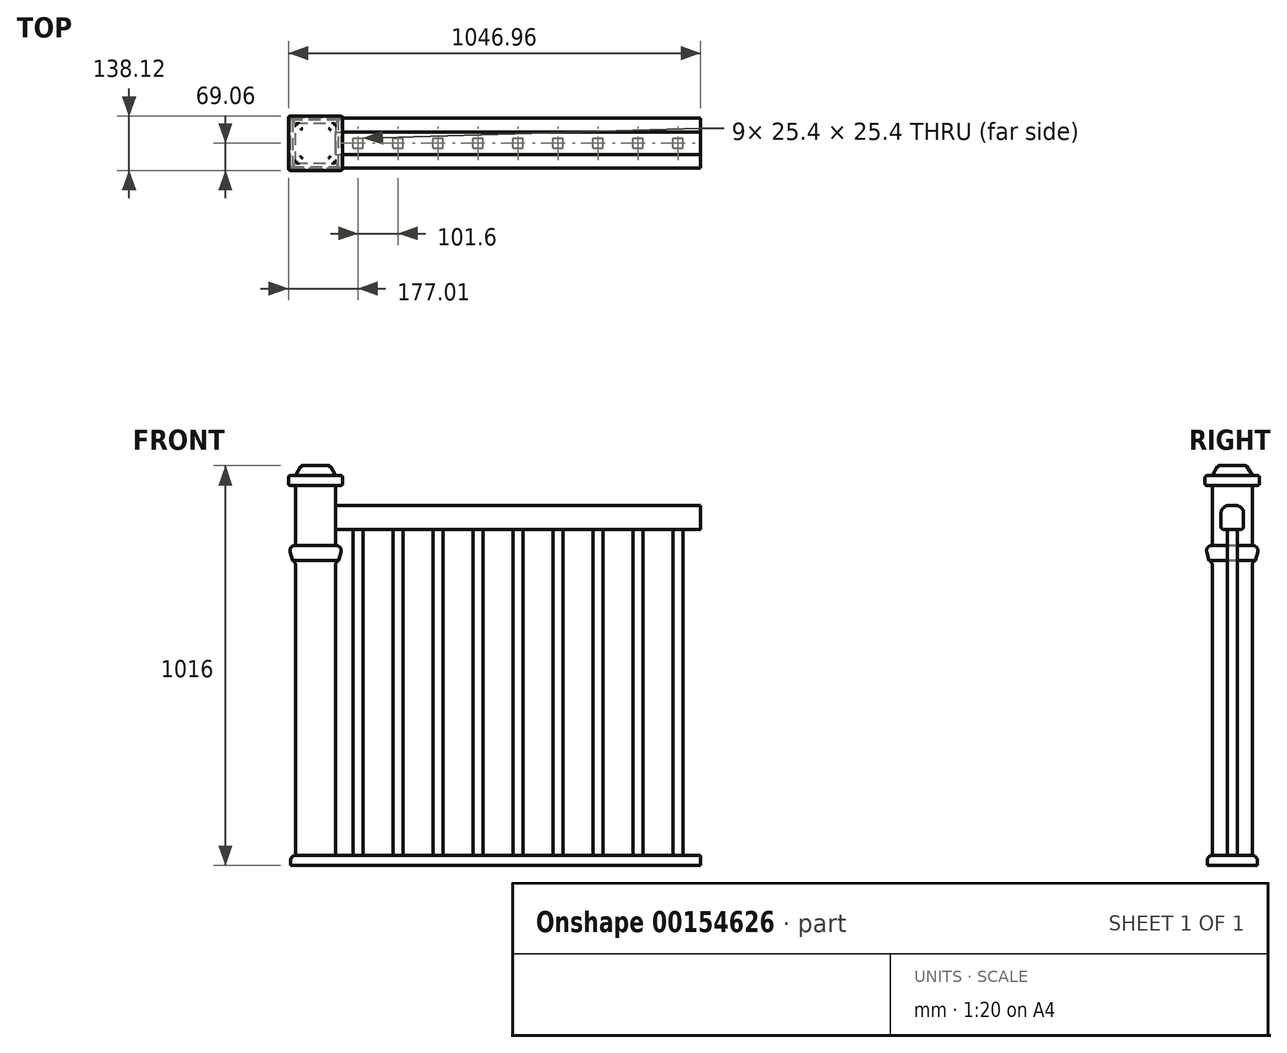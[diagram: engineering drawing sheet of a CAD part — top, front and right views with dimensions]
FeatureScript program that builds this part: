
annotation { "Feature Type Name" : "Feature", "Feature Type Description" : "" }
export const myFeature = defineFeature(function(context is Context, id is Id, definition is map)
    precondition{}
    {
        {
            var Q0;
            Q0=qCreatedBy(makeId("Front.planeOp"),FACE);
            var sketch = newSketch(context, id + "F0", { "sketchPlane" : qUnion([Q0])});
            skLineSegment(sketch, "E0", {"start": v(0, 0) * mm, "end": v(0, 787.4) * mm, "construction": true});
            skLineSegment(sketch, "E1", {"start": v(0, 787.4) * mm, "end": v(1028.7, 787.4) * mm, "construction": true});
            skLineSegment(sketch, "E2", {"start": v(1028.7, 1191.24) * mm, "end": v(1028.7, 0) * mm, "construction": true});
            skLineSegment(sketch, "E3", {"start": v(0, 0) * mm, "end": v(1028.7, 0) * mm, "construction": true});
            skLineSegment(sketch, "E4", {"start": v(1028.7, 1191.24) * mm, "end": v(1247.94, 1191.24) * mm, "construction": true});
            skLineSegment(sketch, "E5", {"start": v(1247.94, 0) * mm, "end": v(1247.94, 1191.24) * mm, "construction": true});
            skLineSegment(sketch, "E6", {"start": v(1028.7, 0) * mm, "end": v(1247.94, 0) * mm, "construction": true});
            skSolve(sketch);
        }
        {
            var Q0;
            Q0=qCreatedBy(makeId("Front.planeOp"),FACE);
            var sketch = newSketch(context, id + "F1", { "sketchPlane" : qUnion([Q0])});
            skLineSegment(sketch, "E7", {"start": v(101.6, 0) * mm, "end": v(0, 0) * mm});
            skLineSegment(sketch, "E8", {"start": v(101.6, 25.4) * mm, "end": v(101.6, 990.6) * mm});
            skLineSegment(sketch, "E9", {"start": v(101.6, 990.6) * mm, "end": v(0, 990.6) * mm});
            skLineSegment(sketch, "E10", {"start": v(0, 990.6) * mm, "end": v(0, 25.4) * mm});
            skLineSegment(sketch, "E11", {"start": v(101.6, 854.08) * mm, "end": v(1028.7, 854.08) * mm});
            skLineSegment(sketch, "E12.0", {"start": v(101.6, 914.4) * mm, "end": v(1028.7, 914.4) * mm});
            skLineSegment(sketch, "E13", {"start": v(1028.7, 914.4) * mm, "end": v(1028.7, 854.08) * mm});
            skLineSegment(sketch, "E14.bottom", {"start": v(-12.7, 25.4) * mm, "end": v(1028.7, 25.4) * mm});
            skLineSegment(sketch, "E14.top", {"start": v(-12.7, 0) * mm, "end": v(1028.7, 0) * mm});
            skLineSegment(sketch, "E14.left", {"start": v(-12.7, 25.4) * mm, "end": v(-12.7, 0) * mm});
            skLineSegment(sketch, "E14.right", {"start": v(1028.7, 25.4) * mm, "end": v(1028.7, 0) * mm});
            skLineSegment(sketch, "E15", {"start": v(146.05, 854.08) * mm, "end": v(146.05, 25.4) * mm});
            skLineSegment(sketch, "E16", {"start": v(171.45, 854.08) * mm, "end": v(171.45, 25.4) * mm});
            skLineSegment(sketch, "E17", {"start": v(247.65, 854.08) * mm, "end": v(247.65, 25.4) * mm});
            skLineSegment(sketch, "E18", {"start": v(273.05, 854.08) * mm, "end": v(273.05, 25.4) * mm});
            skLineSegment(sketch, "E19.direction1", {"start": v(146.05, 25.4) * mm, "end": v(1028.7, 25.4) * mm, "construction": true});
            skLineSegment(sketch, "E20.1.0.0", {"start": v(374.65, 854.08) * mm, "end": v(374.65, 25.4) * mm});
            skLineSegment(sketch, "E20.1.0.1", {"start": v(349.25, 854.08) * mm, "end": v(349.25, 25.4) * mm});
            skLineSegment(sketch, "E20.2.0.0", {"start": v(476.25, 854.08) * mm, "end": v(476.25, 25.4) * mm});
            skLineSegment(sketch, "E20.2.0.1", {"start": v(450.85, 854.08) * mm, "end": v(450.85, 25.4) * mm});
            skLineSegment(sketch, "E20.3.0.0", {"start": v(577.85, 854.08) * mm, "end": v(577.85, 25.4) * mm});
            skLineSegment(sketch, "E20.3.0.1", {"start": v(552.45, 854.08) * mm, "end": v(552.45, 25.4) * mm});
            skLineSegment(sketch, "E20.4.0.0", {"start": v(679.45, 854.08) * mm, "end": v(679.45, 25.4) * mm});
            skLineSegment(sketch, "E20.4.0.1", {"start": v(654.05, 854.08) * mm, "end": v(654.05, 25.4) * mm});
            skLineSegment(sketch, "E20.5.0.0", {"start": v(781.05, 854.08) * mm, "end": v(781.05, 25.4) * mm});
            skLineSegment(sketch, "E20.5.0.1", {"start": v(755.65, 854.08) * mm, "end": v(755.65, 25.4) * mm});
            skLineSegment(sketch, "E20.6.0.0", {"start": v(882.65, 854.08) * mm, "end": v(882.65, 25.4) * mm});
            skLineSegment(sketch, "E20.6.0.1", {"start": v(857.25, 854.08) * mm, "end": v(857.25, 25.4) * mm});
            skLineSegment(sketch, "E20.7.0.0", {"start": v(984.25, 854.08) * mm, "end": v(984.25, 25.4) * mm});
            skLineSegment(sketch, "E20.7.0.1", {"start": v(958.85, 854.08) * mm, "end": v(958.85, 25.4) * mm});
            skLineSegment(sketch, "E20.direction1", {"start": v(247.65, 25.4) * mm, "end": v(349.25, 25.4) * mm, "construction": true});
            skSolve(sketch);
        }
        {
            var Q0;
            {var subQ0=sQuery(id+"F1.wireOp",EDGE,"E9");Q0=makeQuery(id+"F1.imprint","IMPRINT",FACE,{"disambiguationData":[TD([[makeQuery(id+"F1.imprint","IMPRINT",EDGE,{"derivedFrom":subQ0}),1.0]])]});}
            extrude(context, id + "F2", {"entities" : qUnion([Q0]), "endBound" : BoundingType.SYMMETRIC, "depth" : 101.6 * mm});
        }
        {
            var Q0;
            {var subQ25=sQuery(id+"F1.wireOp",EDGE,"E12.0");Q0=makeQuery(id+"F1.imprint","IMPRINT",FACE,{"disambiguationData":[TD([[makeQuery(id+"F1.imprint","IMPRINT",EDGE,{"derivedFrom":subQ25}),-1.0]])]});}
            extrude(context, id + "F3", {"entities" : qUnion([Q0]), "operationType" : NewBodyOperationType.ADD, "depth" : 25.4 * mm});
        }
        {
            var Q0;
            Q0=makeQuery(id+"F2.opExtrude","SWEPT_BODY",BODY,{"disambiguationData":[OSD([sQuery(id+"F1.wireOp",EDGE,"E8"),sQuery(id+"F1.wireOp",EDGE,"E9"),sQuery(id+"F1.wireOp",EDGE,"E10"),sQuery(id+"F1.wireOp",EDGE,"E14.bottom")])]});
            deleteBodies(context, id + "F4", {"entities" : qUnion([Q0])});
        }
        {
            var Q0;
            {var subQ0=sQuery(id+"F1.wireOp",EDGE,"E9");Q0=makeQuery(id+"F1.imprint","IMPRINT",FACE,{"disambiguationData":[TD([[makeQuery(id+"F1.imprint","IMPRINT",EDGE,{"derivedFrom":subQ0}),1.0]])]});}
            extrude(context, id + "F5", {"entities" : qUnion([Q0]), "endBound" : BoundingType.SYMMETRIC, "depth" : 101.6 * mm});
        }
        {
            var Q0;
            {var subQ25=sQuery(id+"F1.wireOp",EDGE,"E12.0");Q0=makeQuery(id+"F1.imprint","IMPRINT",FACE,{"disambiguationData":[TD([[makeQuery(id+"F1.imprint","IMPRINT",EDGE,{"derivedFrom":subQ25}),-1.0]])]});}
            extrude(context, id + "F6", {"entities" : qUnion([Q0]), "operationType" : NewBodyOperationType.ADD, "endBound" : BoundingType.SYMMETRIC, "depth" : 57.15 * mm});
        }
        {
            var Q0;
            {var subQ24=sQuery(id+"F1.wireOp",EDGE,"E14.left");Q0=makeQuery(id+"F1.imprint","IMPRINT",FACE,{"disambiguationData":[TD([[makeQuery(id+"F1.imprint","IMPRINT",EDGE,{"derivedFrom":subQ24}),1.0]])]});}
            extrude(context, id + "F7", {"entities" : qUnion([Q0]), "operationType" : NewBodyOperationType.ADD, "endBound" : BoundingType.SYMMETRIC, "depth" : 127 * mm});
        }
        {
            var Q0;
            {var subQ0=sQuery(id+"F1.wireOp",EDGE,"E15");Q0=makeQuery(id+"F1.imprint","IMPRINT",FACE,{"disambiguationData":[TD([[makeQuery(id+"F1.imprint","IMPRINT",EDGE,{"derivedFrom":subQ0}),1.0]])]});}
            var Q1;
            {var subQ0=sQuery(id+"F1.wireOp",EDGE,"E17");Q1=makeQuery(id+"F1.imprint","IMPRINT",FACE,{"disambiguationData":[TD([[makeQuery(id+"F1.imprint","IMPRINT",EDGE,{"derivedFrom":subQ0}),1.0]])]});}
            var Q2;
            {var subQ0=sQuery(id+"F1.wireOp",EDGE,"E20.1.0.0");Q2=makeQuery(id+"F1.imprint","IMPRINT",FACE,{"disambiguationData":[TD([[makeQuery(id+"F1.imprint","IMPRINT",EDGE,{"derivedFrom":subQ0}),-1.0]])]});}
            var Q3;
            {var subQ0=sQuery(id+"F1.wireOp",EDGE,"E20.2.0.0");Q3=makeQuery(id+"F1.imprint","IMPRINT",FACE,{"disambiguationData":[TD([[makeQuery(id+"F1.imprint","IMPRINT",EDGE,{"derivedFrom":subQ0}),-1.0]])]});}
            var Q4;
            {var subQ0=sQuery(id+"F1.wireOp",EDGE,"E20.3.0.0");Q4=makeQuery(id+"F1.imprint","IMPRINT",FACE,{"disambiguationData":[TD([[makeQuery(id+"F1.imprint","IMPRINT",EDGE,{"derivedFrom":subQ0}),-1.0]])]});}
            var Q5;
            {var subQ0=sQuery(id+"F1.wireOp",EDGE,"E20.4.0.0");Q5=makeQuery(id+"F1.imprint","IMPRINT",FACE,{"disambiguationData":[TD([[makeQuery(id+"F1.imprint","IMPRINT",EDGE,{"derivedFrom":subQ0}),-1.0]])]});}
            var Q6;
            {var subQ0=sQuery(id+"F1.wireOp",EDGE,"E20.5.0.0");Q6=makeQuery(id+"F1.imprint","IMPRINT",FACE,{"disambiguationData":[TD([[makeQuery(id+"F1.imprint","IMPRINT",EDGE,{"derivedFrom":subQ0}),-1.0]])]});}
            var Q7;
            {var subQ0=sQuery(id+"F1.wireOp",EDGE,"E20.6.0.0");Q7=makeQuery(id+"F1.imprint","IMPRINT",FACE,{"disambiguationData":[TD([[makeQuery(id+"F1.imprint","IMPRINT",EDGE,{"derivedFrom":subQ0}),-1.0]])]});}
            var Q8;
            {var subQ0=sQuery(id+"F1.wireOp",EDGE,"E20.7.0.0");Q8=makeQuery(id+"F1.imprint","IMPRINT",FACE,{"disambiguationData":[TD([[makeQuery(id+"F1.imprint","IMPRINT",EDGE,{"derivedFrom":subQ0}),-1.0]])]});}
            var Q9;
            {var subQ0=sQuery(id+"F1.wireOp",EDGE,"E20.8.0.0");Q9=makeQuery(id+"F1.imprint","IMPRINT",FACE,{"disambiguationData":[TD([[makeQuery(id+"F1.imprint","IMPRINT",EDGE,{"derivedFrom":subQ0}),-1.0]])]});}
            var Q10;
            {var subQ0=sQuery(id+"F1.wireOp",EDGE,"E20.9.0.0");Q10=makeQuery(id+"F1.imprint","IMPRINT",FACE,{"disambiguationData":[TD([[makeQuery(id+"F1.imprint","IMPRINT",EDGE,{"derivedFrom":subQ0}),-1.0]])]});}
            var Q11;
            {var subQ0=sQuery(id+"F1.wireOp",EDGE,"E20.10.0.0");Q11=makeQuery(id+"F1.imprint","IMPRINT",FACE,{"disambiguationData":[TD([[makeQuery(id+"F1.imprint","IMPRINT",EDGE,{"derivedFrom":subQ0}),-1.0]])]});}
            extrude(context, id + "F8", {"entities" : qUnion([Q0, Q1, Q2, Q3, Q4, Q5, Q6, Q7, Q8, Q9, Q10, Q11]), "operationType" : NewBodyOperationType.ADD, "endBound" : BoundingType.SYMMETRIC, "depth" : 25.4 * mm});
        }
        {
            var Q0;
            Q0=makeQuery(id+"F5.opExtrude","SWEPT_FACE",FACE,{"disambiguationData":[OSD([sQuery(id+"F1.wireOp",EDGE,"E9")])]});
            extrude(context, id + "F18", {"entities" : qUnion([Q0]), "operationType" : NewBodyOperationType.ADD, "depth" : 25.4 * mm, "hasDraft" : true, "draftAngle" : 30 * degree, "draftPullDirection" : true});
        }
        {
            var Q0;
            {var subQ0=sQuery(id+"F1.wireOp",EDGE,"E9");var subQ1=sQuery(id+"F1.wireOp",EDGE,"E8");var subQ2=makeQuery(id+"F5.opExtrude","CAP_VERTEX",VERTEX,{"disambiguationData":[OSD([subQ1,subQ0])],"isStart":false});Q0=makeQuery(id+"F18.boolean.opBoolean","MERGE",VERTEX,{"derivedFrom":[subQ2,makeQuery(id+"F18.opExtrude","CAP_VERTEX",VERTEX,{"disambiguationData":[OSD([subQ1,subQ0]),TDD([subQ2])],"isStart":true})]});}
            var Q1;
            {var subQ0=sQuery(id+"F1.wireOp",EDGE,"E9");var subQ1=sQuery(id+"F1.wireOp",EDGE,"E8");var subQ2=makeQuery(id+"F5.opExtrude","CAP_VERTEX",VERTEX,{"disambiguationData":[OSD([subQ1,subQ0])],"isStart":true});Q1=makeQuery(id+"F18.boolean.opBoolean","MERGE",VERTEX,{"derivedFrom":[subQ2,makeQuery(id+"F18.opExtrude","CAP_VERTEX",VERTEX,{"disambiguationData":[OSD([subQ1,subQ0]),TDD([subQ2])],"isStart":true})]});}
            var Q2;
            {var subQ0=sQuery(id+"F1.wireOp",EDGE,"E10");var subQ1=sQuery(id+"F1.wireOp",EDGE,"E9");var subQ2=makeQuery(id+"F5.opExtrude","CAP_VERTEX",VERTEX,{"disambiguationData":[OSD([subQ1,subQ0])],"isStart":false});Q2=makeQuery(id+"F18.boolean.opBoolean","MERGE",VERTEX,{"derivedFrom":[subQ2,makeQuery(id+"F18.opExtrude","CAP_VERTEX",VERTEX,{"disambiguationData":[OSD([subQ1,subQ0]),TDD([subQ2])],"isStart":true})]});}
            cPlane(context, id + "F9", {"entities" : qUnion([Q0, Q1, Q2]), "cplaneType" : CPlaneType.THREE_POINT, "offset" : 25.4 * mm, "width" : 152.4 * mm, "height" : 152.4 * mm});
        }
        {
            var Q0;
            Q0=qCreatedBy(id+"F9.planeOp",FACE);
            var sketch = newSketch(context, id + "F19", { "sketchPlane" : qUnion([Q0])});
            skLineSegment(sketch, "E21.bottom", {"start": v(119.86, 69.06) * mm, "end": v(-18.26, 69.06) * mm});
            skLineSegment(sketch, "E21.top", {"start": v(119.86, -69.06) * mm, "end": v(-18.26, -69.06) * mm});
            skLineSegment(sketch, "E21.left", {"start": v(119.86, 69.06) * mm, "end": v(119.86, -69.06) * mm});
            skLineSegment(sketch, "E21.right", {"start": v(-18.26, 69.06) * mm, "end": v(-18.26, -69.06) * mm});
            skPoint(sketch, "E21.middle", {"position": v(50.8, 0) * mm});
            skLineSegment(sketch, "E22", {"start": v(14.66, -36.14) * mm, "end": v(86.94, 36.14) * mm, "construction": true});
            skLineSegment(sketch, "E23", {"start": v(86.94, 36.14) * mm, "end": v(14.66, -36.14) * mm, "construction": true});
            skSolve(sketch);
        }
        {
            var Q0;
            Q0=makeQuery(id+"F19.imprint","IMPRINT",FACE,{"disambiguationData":[TD([[makeQuery(id+"F19.imprint","IMPRINT",EDGE,{"derivedFrom":sQuery(id+"F19.wireOp",EDGE,"E21.bottom")}),1.0]])]});
            extrude(context, id + "F10", {"entities" : qUnion([Q0]), "operationType" : NewBodyOperationType.ADD, "depth" : 25.4 * mm});
        }
        {
            var Q0;
            Q0=makeQuery(id+"F10.opExtrude","CAP_FACE",FACE,{"disambiguationData":[OSD([sQuery(id+"F19.wireOp",EDGE,"E21.bottom"),sQuery(id+"F19.wireOp",EDGE,"E21.top"),sQuery(id+"F19.wireOp",EDGE,"E21.left"),sQuery(id+"F19.wireOp",EDGE,"E21.right")])],"isStart":false});
            cPlane(context, id + "F11", {"entities" : qUnion([Q0]), "cplaneType" : CPlaneType.OFFSET, "offset" : 152.4 * mm, "width" : 152.4 * mm, "height" : 152.4 * mm});
        }
        {
            var Q0;
            Q0=qCreatedBy(id+"F11.planeOp",FACE);
            var sketch = newSketch(context, id + "F12", { "sketchPlane" : qUnion([Q0])});
            skLineSegment(sketch, "E24.bottom", {"start": v(-18.26, 69.06) * mm, "end": v(119.86, 69.06) * mm});
            skLineSegment(sketch, "E24.top", {"start": v(-18.26, -69.06) * mm, "end": v(119.86, -69.06) * mm});
            skLineSegment(sketch, "E24.left", {"start": v(-18.26, 69.06) * mm, "end": v(-18.26, -69.06) * mm});
            skLineSegment(sketch, "E24.right", {"start": v(119.86, 69.06) * mm, "end": v(119.86, -69.06) * mm});
            skSolve(sketch);
        }
        {
            var Q0;
            Q0 = qSketchRegion(id + "F12", true);
            extrude(context, id + "F13", {"entities" : qUnion([Q0]), "operationType" : NewBodyOperationType.ADD, "depth" : 38.1 * mm, "hasDraft" : true, "draftAngle" : 15 * degree, "draftPullDirection" : true});
        }
        {
            var Q0;
            Q0=makeQuery(id+"F13.boolean.opBoolean","INTERSECT",EDGE,{"derivedFrom":[makeQuery(id+"F5.opExtrude","CAP_FACE",FACE,{"disambiguationData":[OSD([sQuery(id+"F1.wireOp",EDGE,"E8"),sQuery(id+"F1.wireOp",EDGE,"E9"),sQuery(id+"F1.wireOp",EDGE,"E10"),sQuery(id+"F1.wireOp",EDGE,"E14.bottom")])],"isStart":false}),makeQuery(id+"F13.opExtrude","CAP_FACE",FACE,{"disambiguationData":[OSD([sQuery(id+"F12.wireOp",EDGE,"E24.bottom"),sQuery(id+"F12.wireOp",EDGE,"E24.top"),sQuery(id+"F12.wireOp",EDGE,"E24.left"),sQuery(id+"F12.wireOp",EDGE,"E24.right")])],"isStart":false})]});
            var Q1;
            Q1=makeQuery(id+"F13.boolean.opBoolean","INTERSECT",EDGE,{"derivedFrom":[makeQuery(id+"F5.opExtrude","SWEPT_FACE",FACE,{"disambiguationData":[OSD([sQuery(id+"F1.wireOp",EDGE,"E10")])]}),makeQuery(id+"F13.opExtrude","CAP_FACE",FACE,{"disambiguationData":[OSD([sQuery(id+"F12.wireOp",EDGE,"E24.bottom"),sQuery(id+"F12.wireOp",EDGE,"E24.top"),sQuery(id+"F12.wireOp",EDGE,"E24.left"),sQuery(id+"F12.wireOp",EDGE,"E24.right")])],"isStart":false})]});
            var Q2;
            Q2=makeQuery(id+"F13.boolean.opBoolean","INTERSECT",EDGE,{"derivedFrom":[makeQuery(id+"F5.opExtrude","CAP_FACE",FACE,{"disambiguationData":[OSD([sQuery(id+"F1.wireOp",EDGE,"E8"),sQuery(id+"F1.wireOp",EDGE,"E9"),sQuery(id+"F1.wireOp",EDGE,"E10"),sQuery(id+"F1.wireOp",EDGE,"E14.bottom")])],"isStart":true}),makeQuery(id+"F13.opExtrude","CAP_FACE",FACE,{"disambiguationData":[OSD([sQuery(id+"F12.wireOp",EDGE,"E24.bottom"),sQuery(id+"F12.wireOp",EDGE,"E24.top"),sQuery(id+"F12.wireOp",EDGE,"E24.left"),sQuery(id+"F12.wireOp",EDGE,"E24.right")])],"isStart":false})]});
            var Q3;
            Q3=makeQuery(id+"F13.boolean.opBoolean","INTERSECT",EDGE,{"derivedFrom":[makeQuery(id+"F5.opExtrude","SWEPT_FACE",FACE,{"disambiguationData":[OSD([sQuery(id+"F1.wireOp",EDGE,"E8")])]}),makeQuery(id+"F13.opExtrude","CAP_FACE",FACE,{"disambiguationData":[OSD([sQuery(id+"F12.wireOp",EDGE,"E24.bottom"),sQuery(id+"F12.wireOp",EDGE,"E24.top"),sQuery(id+"F12.wireOp",EDGE,"E24.left"),sQuery(id+"F12.wireOp",EDGE,"E24.right")])],"isStart":false})]});
            var Q4;
            Q4=makeQuery(id+"F13.opExtrude","CAP_EDGE",EDGE,{"disambiguationData":[OSD([sQuery(id+"F12.wireOp",EDGE,"E24.bottom")])],"isStart":true});
            var Q5;
            Q5=makeQuery(id+"F13.opExtrude","CAP_EDGE",EDGE,{"disambiguationData":[OSD([sQuery(id+"F12.wireOp",EDGE,"E24.left")])],"isStart":true});
            var Q6;
            Q6=makeQuery(id+"F13.opExtrude","CAP_EDGE",EDGE,{"disambiguationData":[OSD([sQuery(id+"F12.wireOp",EDGE,"E24.top")])],"isStart":true});
            var Q7;
            Q7=makeQuery(id+"F13.opExtrude","CAP_EDGE",EDGE,{"disambiguationData":[OSD([sQuery(id+"F12.wireOp",EDGE,"E24.right")])],"isStart":true});
            fillet(context, id + "F20", {"entities" : qUnion([Q0, Q1, Q2, Q3, Q4, Q5, Q6, Q7]), "radius" : 12.7 * mm, "tangentPropagation" : true, "allowEdgeOverflow" : false});
        }
        {
            var Q0;
            Q0=makeQuery(id+"F18.opExtrude","CAP_EDGE",EDGE,{"disambiguationData":[OSD([sQuery(id+"F1.wireOp",EDGE,"E9"),sQuery(id+"F1.wireOp",EDGE,"E10")])],"isStart":false});
            var Q1;
            {var subQ0=sQuery(id+"F1.wireOp",EDGE,"E9");Q1=makeQuery(id+"F18.opExtrude","CAP_EDGE",EDGE,{"disambiguationData":[OSD([subQ0]),TDD([makeQuery(id+"F5.opExtrude","CAP_EDGE",EDGE,{"disambiguationData":[OSD([subQ0])],"isStart":false})])],"isStart":false});}
            var Q2;
            Q2=makeQuery(id+"F18.opExtrude","CAP_EDGE",EDGE,{"disambiguationData":[OSD([sQuery(id+"F1.wireOp",EDGE,"E8"),sQuery(id+"F1.wireOp",EDGE,"E9")])],"isStart":false});
            var Q3;
            {var subQ0=sQuery(id+"F1.wireOp",EDGE,"E9");Q3=makeQuery(id+"F18.opExtrude","SWEPT_FACE",FACE,{"disambiguationData":[OSD([subQ0]),TDD([makeQuery(id+"F5.opExtrude","CAP_EDGE",EDGE,{"disambiguationData":[OSD([subQ0])],"isStart":true})])]});}
            var Q4;
            {var subQ0=sQuery(id+"F1.wireOp",EDGE,"E9");Q4=makeQuery(id+"F18.opExtrude","SWEPT_FACE",FACE,{"disambiguationData":[OSD([subQ0]),TDD([makeQuery(id+"F5.opExtrude","CAP_EDGE",EDGE,{"disambiguationData":[OSD([subQ0])],"isStart":false})])]});}
            var Q5;
            Q5=makeQuery(id+"F10.opExtrude","CAP_FACE",FACE,{"disambiguationData":[OSD([sQuery(id+"F19.wireOp",EDGE,"E21.bottom"),sQuery(id+"F19.wireOp",EDGE,"E21.top"),sQuery(id+"F19.wireOp",EDGE,"E21.left"),sQuery(id+"F19.wireOp",EDGE,"E21.right")])],"isStart":true});
            var Q6;
            Q6=makeQuery(id+"F10.opExtrude","CAP_FACE",FACE,{"disambiguationData":[OSD([sQuery(id+"F19.wireOp",EDGE,"E21.bottom"),sQuery(id+"F19.wireOp",EDGE,"E21.top"),sQuery(id+"F19.wireOp",EDGE,"E21.left"),sQuery(id+"F19.wireOp",EDGE,"E21.right")])],"isStart":false});
            var Q7;
            Q7=makeQuery(id+"F10.opExtrude","SWEPT_EDGE",EDGE,{"disambiguationData":[OSD([sQuery(id+"F19.wireOp",EDGE,"E21.top"),sQuery(id+"F19.wireOp",EDGE,"E21.right")])]});
            var Q8;
            Q8=makeQuery(id+"F10.opExtrude","SWEPT_FACE",FACE,{"disambiguationData":[OSD([sQuery(id+"F19.wireOp",EDGE,"E21.right")])]});
            var Q9;
            Q9=makeQuery(id+"F10.opExtrude","SWEPT_FACE",FACE,{"disambiguationData":[OSD([sQuery(id+"F19.wireOp",EDGE,"E21.top")])]});
            var Q10;
            Q10=makeQuery(id+"F10.opExtrude","SWEPT_FACE",FACE,{"disambiguationData":[OSD([sQuery(id+"F19.wireOp",EDGE,"E21.left")])]});
            var Q11;
            Q11=makeQuery(id+"F10.opExtrude","SWEPT_FACE",FACE,{"disambiguationData":[OSD([sQuery(id+"F19.wireOp",EDGE,"E21.bottom")])]});
            fillet(context, id + "F14", {"entities" : qUnion([Q0, Q1, Q2, Q3, Q4, Q5, Q6, Q7, Q8, Q9, Q10, Q11]), "radius" : 5.08 * mm, "tangentPropagation" : true, "allowEdgeOverflow" : false});
        }
        {
            var Q0;
            Q0=makeQuery(id+"F6.opExtrude","CAP_EDGE",EDGE,{"disambiguationData":[OSD([sQuery(id+"F1.wireOp",EDGE,"E12.0")])],"isStart":false});
            var Q1;
            Q1=makeQuery(id+"F6.opExtrude","CAP_EDGE",EDGE,{"disambiguationData":[OSD([sQuery(id+"F1.wireOp",EDGE,"E12.0")])],"isStart":true});
            fillet(context, id + "F15", {"entities" : qUnion([Q0, Q1]), "radius" : 19.05 * mm, "tangentPropagation" : true, "allowEdgeOverflow" : false});
        }
        {
            var Q0;
            Q0=makeQuery(id+"F6.opExtrude","CAP_EDGE",EDGE,{"disambiguationData":[OSD([sQuery(id+"F1.wireOp",EDGE,"E11")])],"isStart":false});
            var Q1;
            Q1=makeQuery(id+"F6.opExtrude","CAP_EDGE",EDGE,{"disambiguationData":[OSD([sQuery(id+"F1.wireOp",EDGE,"E11")])],"isStart":true});
            fillet(context, id + "F16", {"entities" : qUnion([Q0, Q1]), "radius" : 6.35 * mm, "tangentPropagation" : true, "allowEdgeOverflow" : false});
        }
        {
            var Q0;
            Q0=makeQuery(id+"F7.opExtrude","SWEPT_EDGE",EDGE,{"disambiguationData":[OSD([sQuery(id+"F1.wireOp",EDGE,"E14.bottom"),sQuery(id+"F1.wireOp",EDGE,"E14.left")])]});
            var Q1;
            Q1=makeQuery(id+"F7.opExtrude","CAP_EDGE",EDGE,{"disambiguationData":[OSD([sQuery(id+"F1.wireOp",EDGE,"E14.bottom")])],"isStart":true});
            var Q2;
            Q2=makeQuery(id+"F7.opExtrude","CAP_EDGE",EDGE,{"disambiguationData":[OSD([sQuery(id+"F1.wireOp",EDGE,"E14.bottom")])],"isStart":false});
            fillet(context, id + "F17", {"entities" : qUnion([Q0, Q1, Q2]), "radius" : 12.7 * mm, "tangentPropagation" : true, "allowEdgeOverflow" : false});
        }
    });
